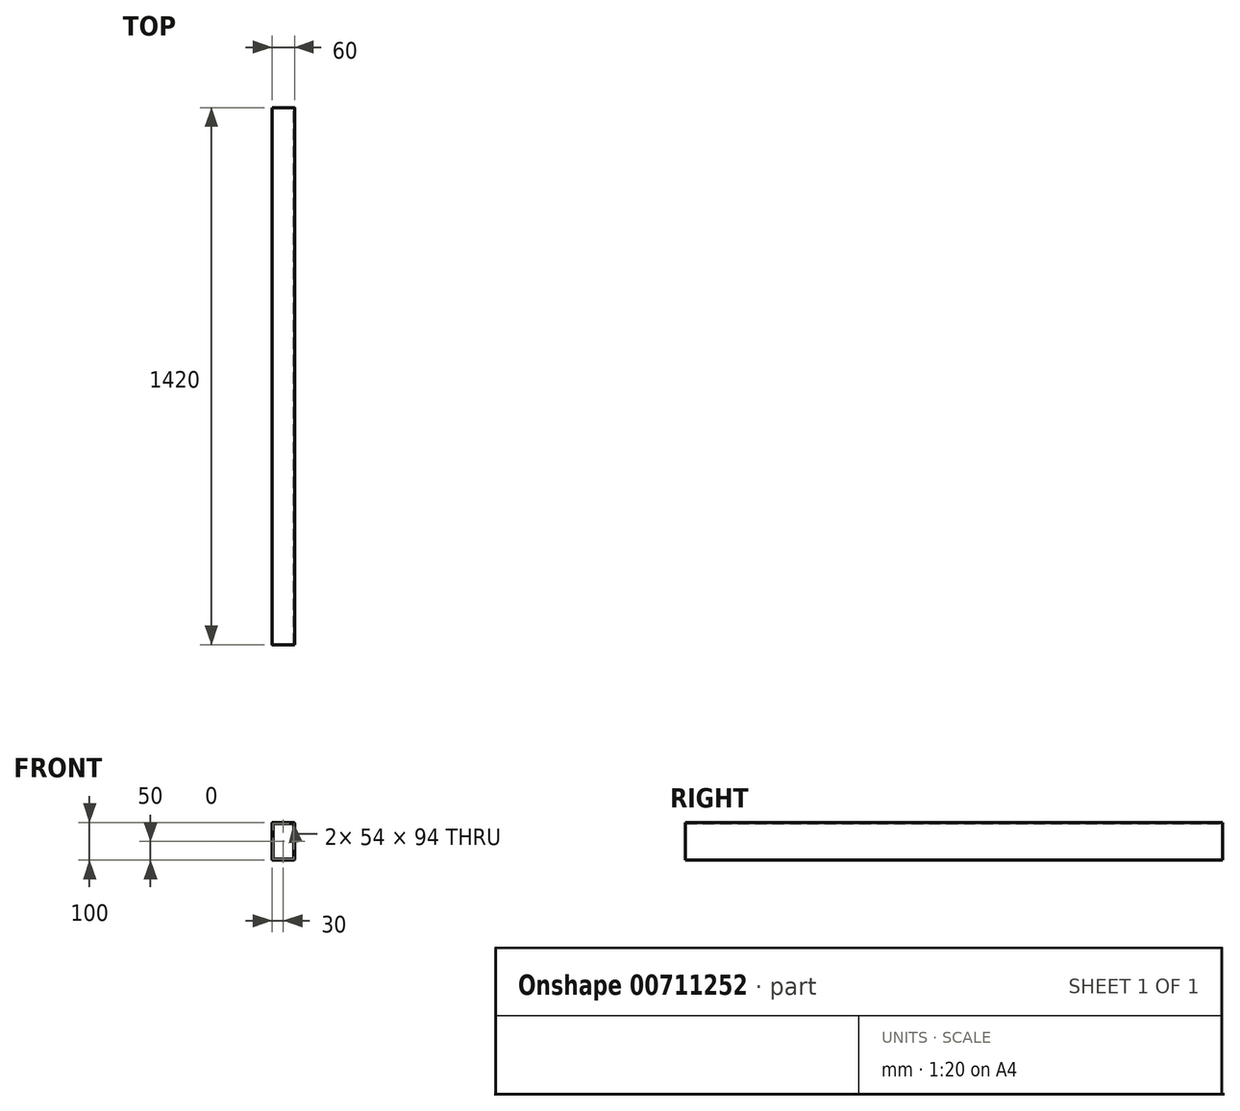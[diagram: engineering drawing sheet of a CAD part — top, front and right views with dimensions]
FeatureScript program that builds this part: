
annotation { "Feature Type Name" : "Feature", "Feature Type Description" : "" }
export const myFeature = defineFeature(function(context is Context, id is Id, definition is map)
    precondition{}
    {
        {
            var Q0;
            Q0=qCreatedBy(makeId("Front.planeOp"),FACE);
            var sketch = newSketch(context, id + "F0", { "sketchPlane" : qUnion([Q0])});
            skLineSegment(sketch, "E0.bottom", {"start": v(27, 50) * mm, "end": v(-27, 50) * mm});
            skLineSegment(sketch, "E0.top", {"start": v(27, -50) * mm, "end": v(-27, -50) * mm});
            skLineSegment(sketch, "E0.left", {"start": v(30, 47) * mm, "end": v(30, -47) * mm});
            skLineSegment(sketch, "E0.right", {"start": v(-30, 47) * mm, "end": v(-30, -47) * mm});
            skPoint(sketch, "E0.middle", {"position": v(0, 0) * mm});
            skPoint(sketch, "E1.visualSharp", {"position": v(-30, 50) * mm});
            skArc(sketch, "E1.filletArc", {"start": v(-27, 50) * mm, "mid": v(-29.12, 49.12) * mm, "end": v(-30, 47) * mm});
            skPoint(sketch, "E2.visualSharp", {"position": v(30, 50) * mm});
            skArc(sketch, "E2.filletArc", {"start": v(30, 47) * mm, "mid": v(29.12, 49.12) * mm, "end": v(27, 50) * mm});
            skPoint(sketch, "E3.visualSharp", {"position": v(30, -50) * mm});
            skArc(sketch, "E3.filletArc", {"start": v(27, -50) * mm, "mid": v(29.12, -49.12) * mm, "end": v(30, -47) * mm});
            skPoint(sketch, "E4.visualSharp", {"position": v(-30, -50) * mm});
            skArc(sketch, "E4.filletArc", {"start": v(-30, -47) * mm, "mid": v(-29.12, -49.12) * mm, "end": v(-27, -50) * mm});
            skLineSegment(sketch, "E5.bottom", {"start": v(27, 47) * mm, "end": v(-27, 47) * mm});
            skLineSegment(sketch, "E5.top", {"start": v(27, -47) * mm, "end": v(-27, -47) * mm});
            skLineSegment(sketch, "E5.left", {"start": v(27, 47) * mm, "end": v(27, -47) * mm});
            skLineSegment(sketch, "E5.right", {"start": v(-27, 47) * mm, "end": v(-27, -47) * mm});
            skSolve(sketch);
        }
        {
            var Q0;
            Q0=makeQuery(id+"F0.imprint","IMPRINT",FACE,{"disambiguationData":[TD([[makeQuery(id+"F0.imprint","IMPRINT",EDGE,{"derivedFrom":sQuery(id+"F0.wireOp",EDGE,"E0.bottom")}),1.0]])]});
            extrude(context, id + "F1", {"entities" : qUnion([Q0]), "depth" : 1420 * mm, "offsetDistance" : 25 * mm});
        }
    });
